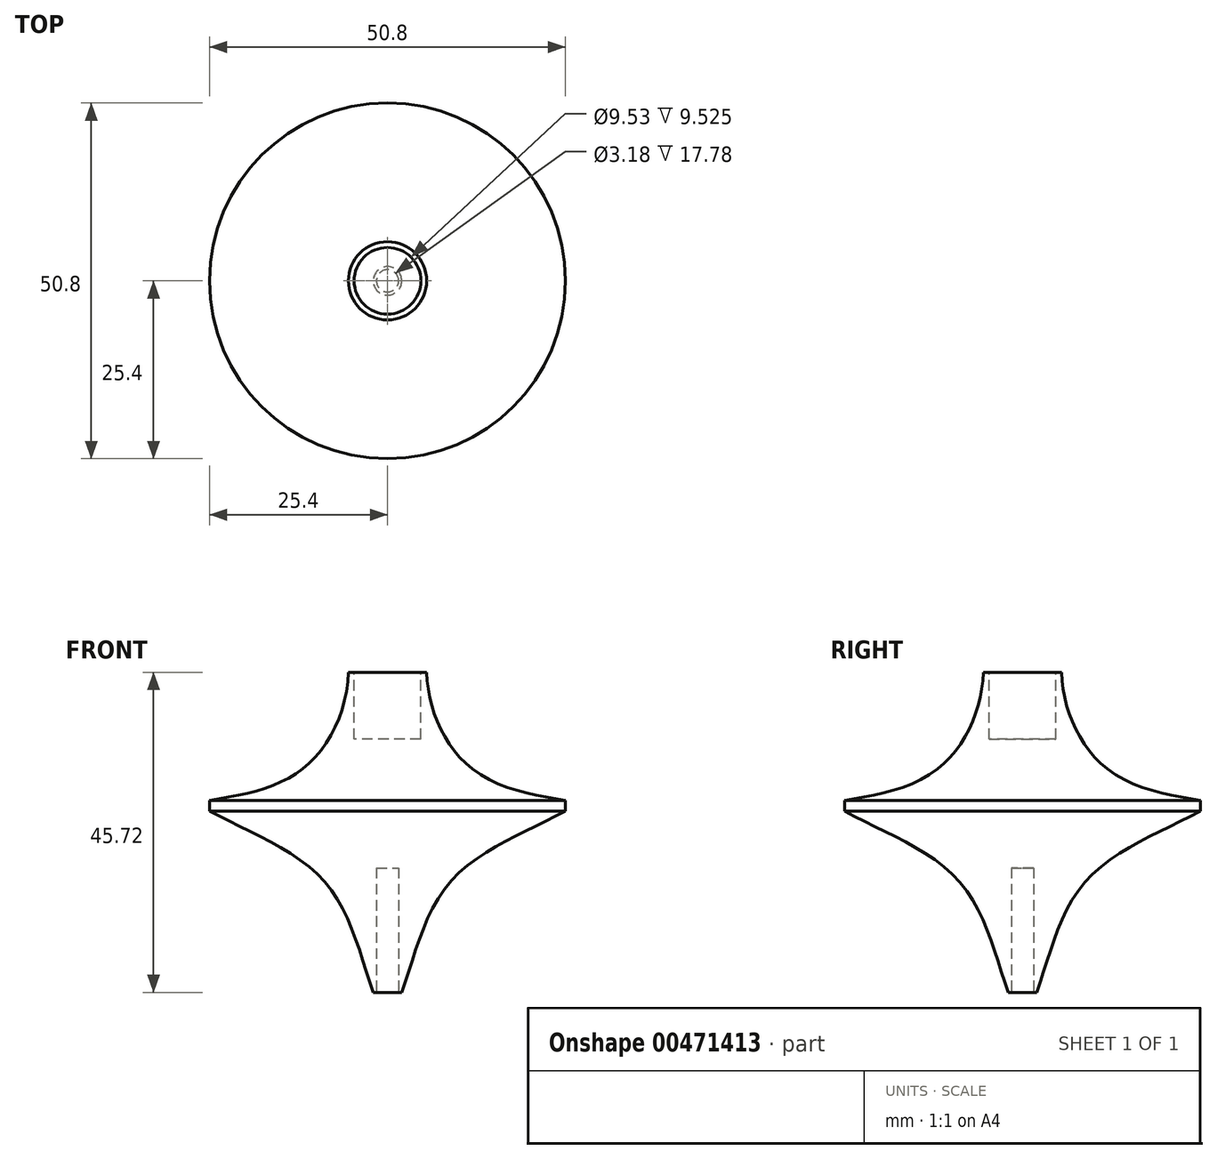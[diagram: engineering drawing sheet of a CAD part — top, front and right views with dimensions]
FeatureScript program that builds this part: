
annotation { "Feature Type Name" : "Feature", "Feature Type Description" : "" }
export const myFeature = defineFeature(function(context is Context, id is Id, definition is map)
    precondition{}
    {
        {
            var Q0;
            Q0=qCreatedBy(makeId("Front.planeOp"),FACE);
            var sketch = newSketch(context, id + "F0", { "sketchPlane" : qUnion([Q0])});
            skLineSegment(sketch, "E0", {"start": v(0, 0) * mm, "end": v(0, 45.72) * mm});
            skLineSegment(sketch, "E1", {"start": v(0, 45.72) * mm, "end": v(5.59, 45.72) * mm});
            skLineSegment(sketch, "E2", {"start": v(25.4, 27.43) * mm, "end": v(25.4, 25.9) * mm});
            skLineSegment(sketch, "E3", {"start": v(0, 0) * mm, "end": v(2.03, 0) * mm});
            skFitSpline(sketch, "E4", {"points": [v(2.03, 0) * mm, v(9.3, 16.16) * mm, v(25.4, 25.9) * mm], "startDerivative": vector(12.06, 34.8) * mm, "endDerivative": vector(30.64, 16.91) * mm});
            skFitSpline(sketch, "E5", {"points": [v(5.59, 45.72) * mm, v(11.67, 32.28) * mm, v(25.4, 27.43) * mm], "startDerivative": vector(1, -31.62) * mm, "endDerivative": vector(32.4, -5.08) * mm});
            skSolve(sketch);
        }
        {
            var Q0;
            Q0=makeQuery(id+"F0.imprint","IMPRINT",FACE,{"disambiguationData":[TD([[makeQuery(id+"F0.imprint","IMPRINT",EDGE,{"derivedFrom":sQuery(id+"F0.wireOp",EDGE,"E0")}),-1.0]])]});
            var Q1;
            Q1=sQuery(id+"F0.wireOp",EDGE,"E0");
            revolve(context, id + "F1", {"entities" : qUnion([Q0]), "axis" : qUnion([Q1]), "revolveType" : RevolveType.FULL});
        }
        {
            var Q0;
            Q0=makeQuery(id+"F1.opRevolve","SWEPT_FACE",FACE,{"disambiguationData":[OSD([sQuery(id+"F0.wireOp",EDGE,"E1")])]});
            var sketch = newSketch(context, id + "F2", { "sketchPlane" : qUnion([Q0])});
            skCircle(sketch, "E6", {"center": v(0, 0) * mm, "radius": 4.76 * mm});
            skSolve(sketch);
        }
        {
            var Q0;
            Q0 = qSketchRegion(id + "F2", true);
            extrude(context, id + "F3", {"entities" : qUnion([Q0]), "operationType" : NewBodyOperationType.REMOVE, "oppositeDirection" : true, "depth" : 9.52 * mm});
        }
        {
            var Q0;
            Q0=makeQuery(id+"F1.opRevolve","SWEPT_FACE",FACE,{"disambiguationData":[OSD([sQuery(id+"F0.wireOp",EDGE,"E3")])]});
            var sketch = newSketch(context, id + "F4", { "sketchPlane" : qUnion([Q0])});
            skCircle(sketch, "E7", {"center": v(0, 0) * mm, "radius": 1.59 * mm});
            skSolve(sketch);
        }
        {
            var Q0;
            Q0=makeQuery(id+"F4.imprint","IMPRINT",FACE,{"disambiguationData":[TD([[makeQuery(id+"F4.imprint","IMPRINT",EDGE,{"derivedFrom":sQuery(id+"F4.wireOp",EDGE,"E7")}),1.0]])]});
            extrude(context, id + "F5", {"entities" : qUnion([Q0]), "operationType" : NewBodyOperationType.REMOVE, "oppositeDirection" : true, "depth" : 17.78 * mm});
        }
    });
